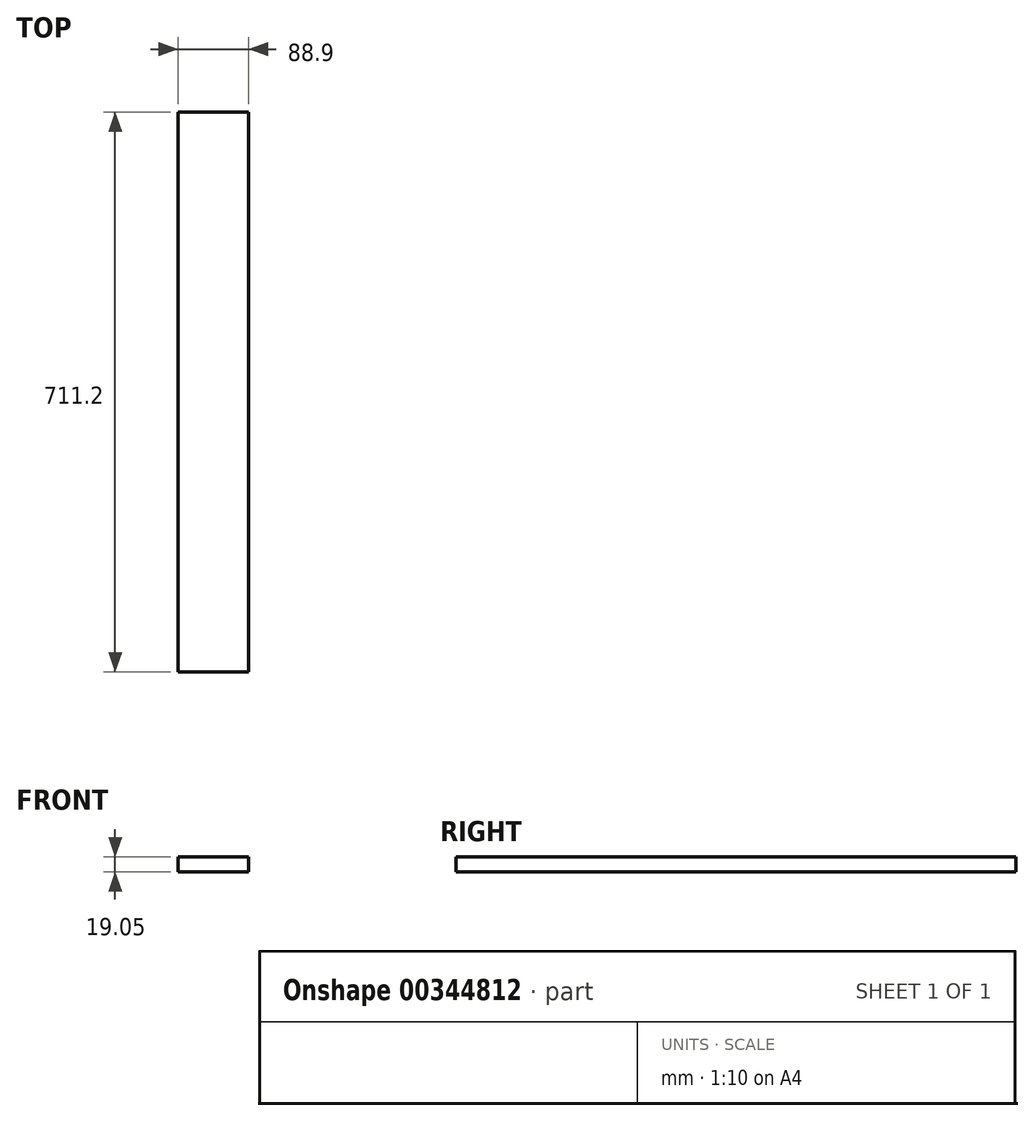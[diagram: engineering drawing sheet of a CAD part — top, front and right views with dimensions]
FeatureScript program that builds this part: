
annotation { "Feature Type Name" : "Feature", "Feature Type Description" : "" }
export const myFeature = defineFeature(function(context is Context, id is Id, definition is map)
    precondition{}
    {
        {
            var Q0;
            Q0=qCreatedBy(makeId("Front.planeOp"),FACE);
            var sketch = newSketch(context, id + "F0", { "sketchPlane" : qUnion([Q0])});
            skLineSegment(sketch, "E0.bottom", {"start": v(0, 0) * mm, "end": v(88.9, 0) * mm});
            skLineSegment(sketch, "E0.top", {"start": v(0, 19.05) * mm, "end": v(88.9, 19.05) * mm});
            skLineSegment(sketch, "E0.left", {"start": v(0, 0) * mm, "end": v(0, 19.05) * mm});
            skLineSegment(sketch, "E0.right", {"start": v(88.9, 0) * mm, "end": v(88.9, 19.05) * mm});
            skSolve(sketch);
        }
        {
            var Q0;
            Q0=makeQuery(id+"F0.imprint","IMPRINT",FACE,{"disambiguationData":[TD([[makeQuery(id+"F0.imprint","IMPRINT",EDGE,{"derivedFrom":sQuery(id+"F0.wireOp",EDGE,"E0.bottom")}),1.0]])]});
            extrude(context, id + "F1", {"entities" : qUnion([Q0]), "depth" : 711.2 * mm});
        }
    });
